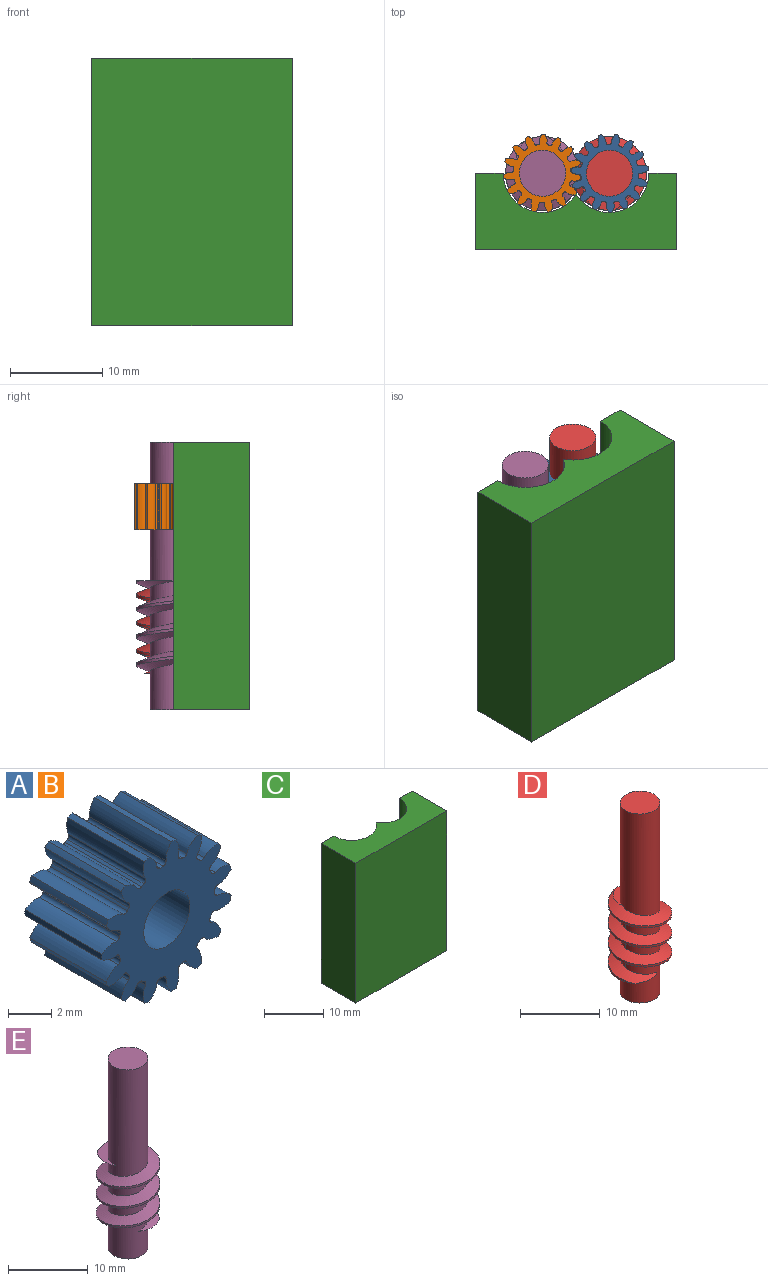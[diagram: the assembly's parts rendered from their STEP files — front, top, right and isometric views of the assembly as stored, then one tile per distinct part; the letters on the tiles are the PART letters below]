
ASSEMBLY  parts=5 mates=4
PART A: 93 faces, bbox 8.4x5x8.5 mm
  f0: cylinder r=4.25mm len=5mm, axis (0,1,0), area 1.6mm2, adj f14,f17,f83,f90
  f1: cylinder r=4.25mm len=5mm, axis (0,1,0), area 1.6mm2, adj f14,f17,f73,f85
  f2: cylinder r=4.25mm len=5mm, axis (0,1,0), area 1.6mm2, adj f14,f17,f18,f80
  f3: cylinder r=4.25mm len=5mm, axis (0,1,0), area 1.6mm2, adj f14,f17,f75,f78
  f4: cylinder r=4.25mm len=5mm, axis (0,1,0), area 1.6mm2, adj f14,f17,f63,f70
  f5: cylinder r=4.25mm len=5mm, axis (0,1,0), area 1.6mm2, adj f14,f17,f65,f88
  f6: cylinder r=4.25mm len=5mm, axis (0,1,0), area 1.6mm2, adj f14,f17,f60,f68
  f7: cylinder r=4.25mm len=5mm, axis (0,1,0), area 1.6mm2, adj f14,f17,f55,f58
  f8: cylinder r=4.25mm len=5mm, axis (0,1,0), area 1.6mm2, adj f14,f17,f38,f50
  f9: cylinder r=4.25mm len=5mm, axis (0,1,0), area 1.6mm2, adj f14,f17,f45,f48
  f10: cylinder r=4.25mm len=5mm, axis (0,1,0), area 1.6mm2, adj f14,f17,f33,f40
  f11: cylinder r=4.25mm len=5mm, axis (0,1,0), area 1.6mm2, adj f14,f17,f23,f35
  f12: cylinder r=4.25mm len=5mm, axis (0,1,0), area 1.6mm2, adj f14,f17,f30,f53
  f13: cylinder r=4.25mm len=5mm, axis (0,1,0), area 1.6mm2, adj f14,f17,f25,f28
  f14: plane 8.49x8.45mm, normal (0,-1,0), area 35.8mm2, adj f0,f1,f2,f3,f4,f5,f6,f7
  f15: cylinder r=1.5mm len=5mm, axis (0,1,0), area 47.1mm2, adj f14,f17
  f16: cylinder r=4.25mm len=5mm, axis (0,1,0), area 1.6mm2, adj f14,f17,f20,f43
  f17: plane 8.49x8.45mm, normal (0,1,0), area 35.8mm2, adj f0,f1,f2,f3,f4,f5,f6,f7
  f18: extruded ~5x0.88mm, area 5mm2, adj f2,f14,f17,f21
  f19: cylinder r=3.12mm len=5mm, axis (0,1,0), area 0.9mm2, adj f14,f17,f21,f22
  f20: extruded ~5x0.88mm, area 5mm2, adj f14,f16,f17,f22
  f21: cylinder r=0.2mm len=5mm, axis (0,1,0), area 1.5mm2, adj f14,f17,f18,f19
  f22: cylinder r=0.2mm len=5mm, axis (0,1,0), area 1.5mm2, adj f14,f17,f19,f20
  f23: extruded ~5x0.97mm, area 5mm2, adj f11,f14,f17,f26
  f24: cylinder r=3.12mm len=5mm, axis (0,1,0), area 0.9mm2, adj f14,f17,f26,f27
  f25: extruded ~5x0.81mm, area 5mm2, adj f13,f14,f17,f27
  f26: cylinder r=0.2mm len=5mm, axis (0,1,0), area 1.5mm2, adj f14,f17,f23,f24
  f27: cylinder r=0.2mm len=5mm, axis (0,1,0), area 1.5mm2, adj f14,f17,f24,f25
  f28: extruded ~5x0.86mm, area 5mm2, adj f13,f14,f17,f31
  f29: cylinder r=3.12mm len=5mm, axis (0,1,0), area 0.9mm2, adj f14,f17,f31,f32
  f30: extruded ~5x0.96mm, area 5mm2, adj f12,f14,f17,f32
  f31: cylinder r=0.2mm len=5mm, axis (0,1,0), area 1.5mm2, adj f14,f17,f28,f29
  f32: cylinder r=0.2mm len=5mm, axis (0,1,0), area 1.5mm2, adj f14,f17,f29,f30
  f33: extruded ~5x0.92mm, area 5mm2, adj f10,f14,f17,f36
  f34: cylinder r=3.12mm len=5mm, axis (0,1,0), area 0.9mm2, adj f14,f17,f36,f37
  f35: extruded ~5x0.83mm, area 5mm2, adj f11,f14,f17,f37
  f36: cylinder r=0.2mm len=5mm, axis (0,1,0), area 1.5mm2, adj f14,f17,f33,f34
  f37: cylinder r=0.2mm len=5mm, axis (0,1,0), area 1.5mm2, adj f14,f17,f34,f35
  f38: extruded ~5x0.7mm, area 5mm2, adj f8,f14,f17,f41
  f39: cylinder r=3.12mm len=5mm, axis (0,1,0), area 0.9mm2, adj f14,f17,f41,f42
  f40: extruded ~5x0.97mm, area 5mm2, adj f10,f14,f17,f42
  f41: cylinder r=0.2mm len=5mm, axis (0,1,0), area 1.5mm2, adj f14,f17,f38,f39
  f42: cylinder r=0.2mm len=5mm, axis (0,1,0), area 1.5mm2, adj f14,f17,f39,f40
  f43: extruded ~5x0.97mm, area 5mm2, adj f14,f16,f17,f46
  f44: cylinder r=3.12mm len=5mm, axis (0,1,0), area 0.9mm2, adj f14,f17,f46,f47
  f45: extruded ~5x0.75mm, area 5mm2, adj f9,f14,f17,f47
  f46: cylinder r=0.2mm len=5mm, axis (0,1,0), area 1.5mm2, adj f14,f17,f43,f44
  f47: cylinder r=0.2mm len=5mm, axis (0,1,0), area 1.5mm2, adj f14,f17,f44,f45
  f48: extruded ~5x0.9mm, area 5mm2, adj f9,f14,f17,f51
  f49: cylinder r=3.12mm len=5mm, axis (0,1,0), area 0.9mm2, adj f14,f17,f51,f52
  f50: extruded ~5x0.94mm, area 5mm2, adj f8,f14,f17,f52
  f51: cylinder r=0.2mm len=5mm, axis (0,1,0), area 1.5mm2, adj f14,f17,f48,f49
  f52: cylinder r=0.2mm len=5mm, axis (0,1,0), area 1.5mm2, adj f14,f17,f49,f50
  f53: extruded ~5x0.77mm, area 5mm2, adj f12,f14,f17,f56
  f54: cylinder r=3.12mm len=5mm, axis (0,1,0), area 0.9mm2, adj f14,f17,f56,f57
  f55: extruded ~5x0.95mm, area 5mm2, adj f7,f14,f17,f57
  f56: cylinder r=0.2mm len=5mm, axis (0,1,0), area 1.5mm2, adj f14,f17,f53,f54
  f57: cylinder r=0.2mm len=5mm, axis (0,1,0), area 1.5mm2, adj f14,f17,f54,f55
  f58: extruded ~5x0.95mm, area 5mm2, adj f7,f14,f17,f61
  f59: cylinder r=3.12mm len=5mm, axis (0,1,0), area 0.9mm2, adj f14,f17,f61,f62
  f60: extruded ~5x0.77mm, area 5mm2, adj f6,f14,f17,f62
  f61: cylinder r=0.2mm len=5mm, axis (0,1,0), area 1.5mm2, adj f14,f17,f58,f59
  f62: cylinder r=0.2mm len=5mm, axis (0,1,0), area 1.5mm2, adj f14,f17,f59,f60
  f63: extruded ~5x0.81mm, area 5mm2, adj f4,f14,f17,f66
  f64: cylinder r=3.12mm len=5mm, axis (0,1,0), area 0.9mm2, adj f14,f17,f66,f67
  f65: extruded ~5x0.97mm, area 5mm2, adj f5,f14,f17,f67
  f66: cylinder r=0.2mm len=5mm, axis (0,1,0), area 1.5mm2, adj f14,f17,f63,f64
  f67: cylinder r=0.2mm len=5mm, axis (0,1,0), area 1.5mm2, adj f14,f17,f64,f65
  f68: extruded ~5x0.96mm, area 5mm2, adj f6,f14,f17,f71
  f69: cylinder r=3.12mm len=5mm, axis (0,1,0), area 0.9mm2, adj f14,f17,f71,f72
  f70: extruded ~5x0.86mm, area 5mm2, adj f4,f14,f17,f72
  f71: cylinder r=0.2mm len=5mm, axis (0,1,0), area 1.5mm2, adj f14,f17,f68,f69
  f72: cylinder r=0.2mm len=5mm, axis (0,1,0), area 1.5mm2, adj f14,f17,f69,f70
  f73: extruded ~5x0.94mm, area 5mm2, adj f1,f14,f17,f76
  f74: cylinder r=3.12mm len=5mm, axis (0,1,0), area 0.9mm2, adj f14,f17,f76,f77
  f75: extruded ~5x0.9mm, area 5mm2, adj f3,f14,f17,f77
  f76: cylinder r=0.2mm len=5mm, axis (0,1,0), area 1.5mm2, adj f14,f17,f73,f74
  f77: cylinder r=0.2mm len=5mm, axis (0,1,0), area 1.5mm2, adj f14,f17,f74,f75
  f78: extruded ~5x0.75mm, area 5mm2, adj f3,f14,f17,f81
  f79: cylinder r=3.12mm len=5mm, axis (0,1,0), area 0.9mm2, adj f14,f17,f81,f82
  f80: extruded ~5x0.97mm, area 5mm2, adj f2,f14,f17,f82
  f81: cylinder r=0.2mm len=5mm, axis (0,1,0), area 1.5mm2, adj f14,f17,f78,f79
  f82: cylinder r=0.2mm len=5mm, axis (0,1,0), area 1.5mm2, adj f14,f17,f79,f80
  f83: extruded ~5x0.97mm, area 5mm2, adj f0,f14,f17,f86
  f84: cylinder r=3.12mm len=5mm, axis (0,1,0), area 0.9mm2, adj f14,f17,f86,f87
  f85: extruded ~5x0.7mm, area 5mm2, adj f1,f14,f17,f87
  f86: cylinder r=0.2mm len=5mm, axis (0,1,0), area 1.5mm2, adj f14,f17,f83,f84
  f87: cylinder r=0.2mm len=5mm, axis (0,1,0), area 1.5mm2, adj f14,f17,f84,f85
  f88: extruded ~5x0.83mm, area 5mm2, adj f5,f14,f17,f91
  f89: cylinder r=3.12mm len=5mm, axis (0,1,0), area 0.9mm2, adj f14,f17,f91,f92
  f90: extruded ~5x0.92mm, area 5mm2, adj f0,f14,f17,f92
  f91: cylinder r=0.2mm len=5mm, axis (0,1,0), area 1.5mm2, adj f14,f17,f88,f89
  f92: cylinder r=0.2mm len=5mm, axis (0,1,0), area 1.5mm2, adj f14,f17,f89,f90
PART B: same geometry as A
PART C: 9 faces, bbox 21.8x8.3x29 mm
  f0: plane 29x21.75mm, normal (0,-1,0), area 630.8mm2, adj f1,f2,f4,f5
  f1: plane 21.75x8.25mm, normal (0,0,1), area 124.6mm2, adj f0,f3,f4,f5,f6,f7,f8
  f2: plane 21.75x8.25mm, normal (0,0,-1), area 124.6mm2, adj f0,f3,f4,f5,f6,f7,f8
  f3: cylinder r=4.25mm len=29mm, axis (0,0,-1), area 319.5mm2, adj f1,f2,f6,f7
  f4: plane 29x8.25mm, normal (1,0,0), area 239.3mm2, adj f0,f1,f2,f7
  f5: plane 29x8.25mm, normal (-1,0,0), area 239.3mm2, adj f0,f1,f2,f8
  f6: cylinder r=4.25mm len=29mm, axis (0,0,-1), area 319.5mm2, adj f1,f2,f3,f8
  f7: plane 29x3mm, normal (0,1,0), area 87mm2, adj f1,f2,f3,f4
  f8: plane 29x3mm, normal (0,1,0), area 87mm2, adj f1,f2,f5,f6
PART D: 11 faces, bbox 8.5x9.7x29.5 mm
  f0: bspline ~12.35x9.24mm, area 109.7mm2, adj f2,f3,f4,f5,f6,f7,f8
  f1: bspline ~12.35x9.24mm, area 110.1mm2, adj f2,f3,f4,f5,f6,f7,f8
  f2: cylinder r=4mm len=10mm, axis (0,0,-1), area 25.4mm2, adj f0,f1,f3,f4
  f3: plane 5.81x4.81mm, normal (0,0,1), area 8.4mm2, adj f0,f1,f2,f5
  f4: plane 5.84x5.02mm, normal (0,0,-1), area 8.4mm2, adj f0,f1,f2,f6
  f5: cylinder r=2.5mm len=18.14mm, axis (0,0,-1), area 255mm2, adj f0,f1,f3,f7,f9
  f6: cylinder r=2.5mm len=6.44mm, axis (0,0,-1), area 76.4mm2, adj f0,f1,f4,f8,f10
  f7: cylinder r=2.5mm len=5mm, axis (0,0,-1), area 24.7mm2, adj f0,f1,f5,f8
  f8: cylinder r=2.5mm len=5mm, axis (0,0,-1), area 24.7mm2, adj f0,f1,f6,f7
  f9: plane 5x5mm, normal (0,0,1), area 19.6mm2, adj f5
  f10: plane 5x5mm, normal (0,0,-1), area 19.6mm2, adj f6
PART E: 11 faces, bbox 8.5x9.7x29.5 mm
  f0: bspline ~12.35x9.24mm, area 109.7mm2, adj f2,f3,f4,f5,f6,f7,f8
  f1: bspline ~12.35x9.24mm, area 110.1mm2, adj f2,f3,f4,f5,f6,f7,f8
  f2: cylinder r=4mm len=10mm, axis (0,0,-1), area 24.5mm2, adj f0,f1,f3,f4
  f3: plane 5.81x4.81mm, normal (0,0,1), area 8.4mm2, adj f0,f1,f2,f5
  f4: plane 5.84x5.02mm, normal (0,0,-1), area 8.4mm2, adj f0,f1,f2,f6
  f5: cylinder r=2.5mm len=18.14mm, axis (0,0,-1), area 255mm2, adj f0,f1,f3,f7,f9
  f6: cylinder r=2.5mm len=6.44mm, axis (0,0,-1), area 76.4mm2, adj f0,f1,f4,f8,f10
  f7: cylinder r=2.5mm len=5mm, axis (0,0,-1), area 24.7mm2, adj f0,f1,f5,f8
  f8: cylinder r=2.5mm len=5mm, axis (0,0,-1), area 24.8mm2, adj f0,f1,f6,f7
  f9: plane 5x5mm, normal (0,0,1), area 19.6mm2, adj f5
  f10: plane 5x5mm, normal (0,0,-1), area 19.6mm2, adj f6
PLACE A rot(axis=(-0.57,-0.58,0.58),120.8deg) t=(5.17,6.08,13.79)mm
PLACE B rot(axis=(-0.97,0.17,-0.17),91.6deg) t=(-2.08,6.08,13.79)mm
PLACE C t=(1.55,6.08,-5.71)mm fixed
PLACE D rot(axis=(0,0,-1),178.6deg) t=(25.17,6.56,-1.71)mm
PLACE E rot(axis=(0,0,-1),1.4deg) t=(-2.08,6.08,-1.71)mm
MATE fastened B.f0 <-> E.f5  axis (0,0,1) through (-2.08,6.08,18.79)mm
MATE revolute E.f5 <-> C.f6  axis (0,0,1) through (-2.08,6.08,23.29)mm
MATE revolute D.f5 <-> C.f3  axis (0,0,-1) through (5.17,6.08,23.29)mm
MATE fastened A.f0 <-> D.f5  axis (0,0,1) through (5.17,6.08,18.79)mm
